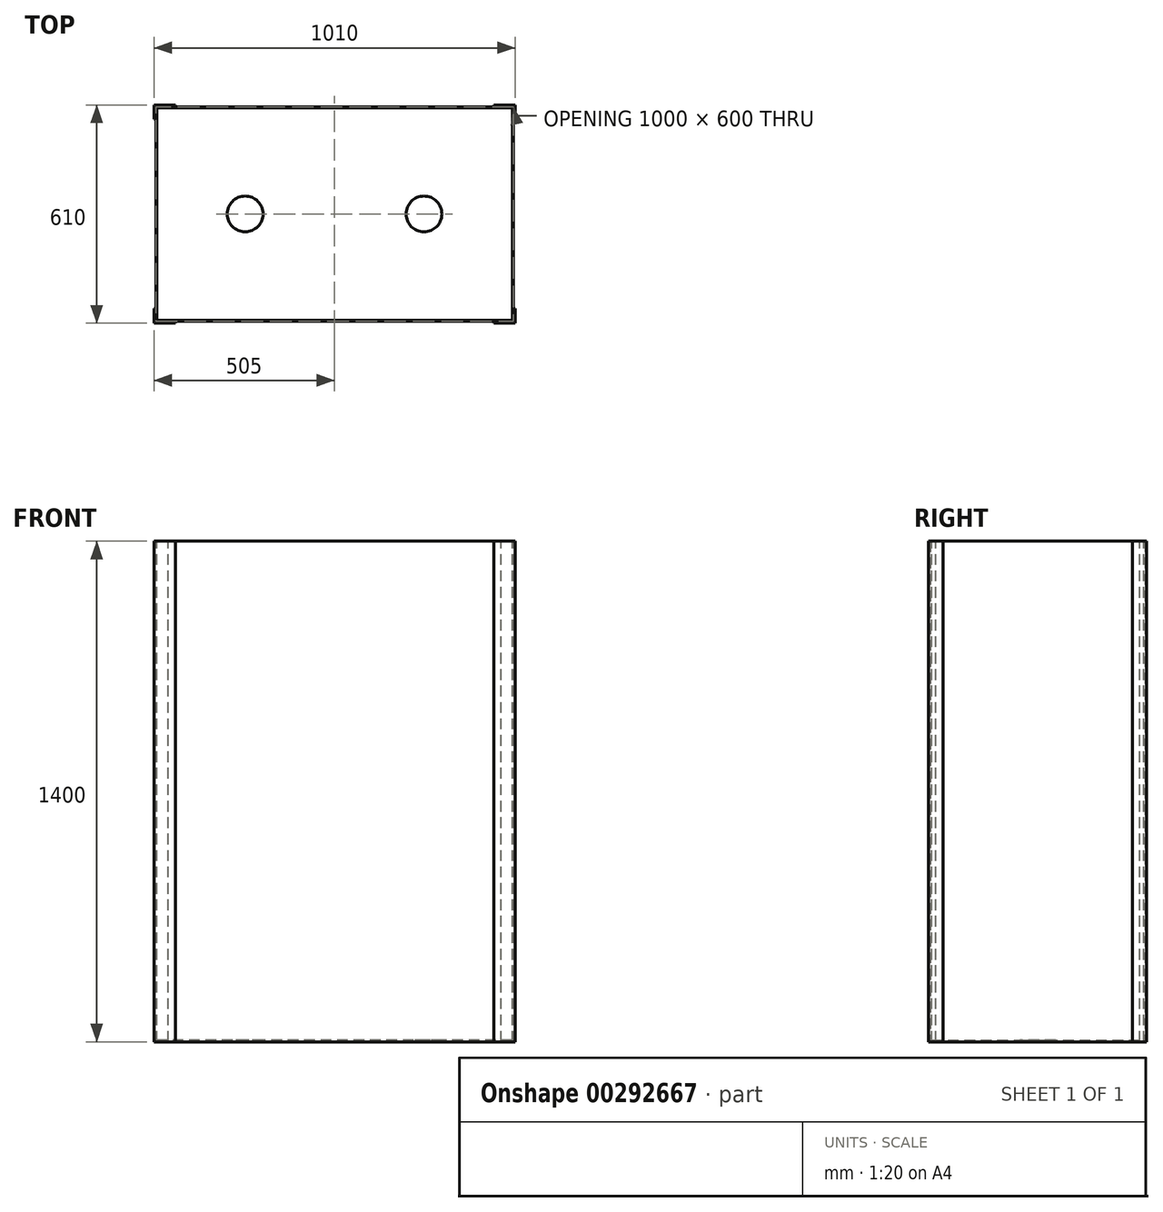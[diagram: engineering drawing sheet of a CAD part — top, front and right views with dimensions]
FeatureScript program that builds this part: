
annotation { "Feature Type Name" : "Feature", "Feature Type Description" : "" }
export const myFeature = defineFeature(function(context is Context, id is Id, definition is map)
    precondition{}
    {
        {
            var Q0;
            Q0=qCreatedBy(makeId("Top.planeOp"),FACE);
            cPlane(context, id + "F0", {"entities" : qUnion([Q0]), "cplaneType" : CPlaneType.OFFSET, "offset" : 1400 * mm, "width" : 150 * mm, "height" : 150 * mm});
        }
        {
            var Q0;
            Q0=qCreatedBy(makeId("Top.planeOp"),FACE);
            var sketch = newSketch(context, id + "F1", { "sketchPlane" : qUnion([Q0])});
            skLineSegment(sketch, "E0.bottom", {"start": v(500, 300) * mm, "end": v(-500, 300) * mm, "construction": true});
            skLineSegment(sketch, "E0.top", {"start": v(500, -300) * mm, "end": v(-500, -300) * mm, "construction": true});
            skLineSegment(sketch, "E0.left", {"start": v(500, 300) * mm, "end": v(500, -300) * mm, "construction": true});
            skLineSegment(sketch, "E0.right", {"start": v(-500, 300) * mm, "end": v(-500, -300) * mm, "construction": true});
            skPoint(sketch, "E0.middle", {"position": v(0, 0) * mm});
            skLineSegment(sketch, "E1", {"start": v(-505, 265) * mm, "end": v(-505, 305) * mm});
            skLineSegment(sketch, "E2", {"start": v(-505, 305) * mm, "end": v(-445, 305) * mm});
            skLineSegment(sketch, "E3.0", {"start": v(-500, 300) * mm, "end": v(-445, 300) * mm});
            skLineSegment(sketch, "E3.1", {"start": v(-500, 265) * mm, "end": v(-500, 300) * mm});
            skLineSegment(sketch, "E4", {"start": v(-445, 305) * mm, "end": v(-445, 300) * mm});
            skLineSegment(sketch, "E5", {"start": v(-505, 265) * mm, "end": v(-500, 265) * mm});
            skLineSegment(sketch, "E6", {"start": v(0, 0) * mm, "end": v(0, 347.4) * mm, "construction": true});
            skLineSegment(sketch, "E7", {"start": v(0, 0) * mm, "end": v(-536.75, 0) * mm, "construction": true});
            skPoint(sketch, "E7.endSnap0", {"position": v(-500, 0) * mm});
            skLineSegment(sketch, "E8.MirrorCS", {"start": v(445, 305) * mm, "end": v(445, 300) * mm});
            skLineSegment(sketch, "E9.MirrorCS", {"start": v(505, 265) * mm, "end": v(500, 265) * mm});
            skLineSegment(sketch, "E10.MirrorCS", {"start": v(500, 265) * mm, "end": v(500, 300) * mm});
            skLineSegment(sketch, "E11.MirrorCS", {"start": v(505, 265) * mm, "end": v(505, 305) * mm});
            skLineSegment(sketch, "E12.MirrorCS", {"start": v(505, 305) * mm, "end": v(445, 305) * mm});
            skLineSegment(sketch, "E13.MirrorCS", {"start": v(500, 300) * mm, "end": v(445, 300) * mm});
            skLineSegment(sketch, "E14.MirrorCS", {"start": v(445, -305) * mm, "end": v(445, -300) * mm});
            skLineSegment(sketch, "E15.MirrorCS", {"start": v(-505, -265) * mm, "end": v(-500, -265) * mm});
            skLineSegment(sketch, "E16.MirrorCS", {"start": v(-445, -305) * mm, "end": v(-445, -300) * mm});
            skLineSegment(sketch, "E17.MirrorCS", {"start": v(505, -265) * mm, "end": v(500, -265) * mm});
            skLineSegment(sketch, "E18.MirrorCS", {"start": v(-500, -300) * mm, "end": v(-445, -300) * mm});
            skLineSegment(sketch, "E19.MirrorCS", {"start": v(-505, -265) * mm, "end": v(-505, -305) * mm});
            skLineSegment(sketch, "E20.MirrorCS", {"start": v(500, -300) * mm, "end": v(445, -300) * mm});
            skLineSegment(sketch, "E21.MirrorCS", {"start": v(-505, -305) * mm, "end": v(-445, -305) * mm});
            skLineSegment(sketch, "E22.MirrorCS", {"start": v(505, -265) * mm, "end": v(505, -305) * mm});
            skLineSegment(sketch, "E23.MirrorCS", {"start": v(500, -265) * mm, "end": v(500, -300) * mm});
            skLineSegment(sketch, "E24.MirrorCS", {"start": v(505, -305) * mm, "end": v(445, -305) * mm});
            skLineSegment(sketch, "E25.MirrorCS", {"start": v(-500, -265) * mm, "end": v(-500, -300) * mm});
            skSolve(sketch);
        }
        {
            var Q0;
            Q0 = qSketchRegion(id + "F1", true);
            var Q1;
            Q1=qCreatedBy(id+"F0.planeOp",FACE);
            extrude(context, id + "F2", {"entities" : qUnion([Q0]), "endBound" : BoundingType.UP_TO_SURFACE, "endBoundEntityFace" : qUnion([Q1]), "depth" : 100 * mm});
        }
        {
            var Q0;
            Q0=qCreatedBy(id+"F0.planeOp",FACE);
            var sketch = newSketch(context, id + "F3", { "sketchPlane" : qUnion([Q0])});
            skLineSegment(sketch, "E26.bottom", {"start": v(-465, 300) * mm, "end": v(465, 300) * mm});
            skLineSegment(sketch, "E26.top", {"start": v(-465, 297) * mm, "end": v(465, 297) * mm});
            skLineSegment(sketch, "E26.left", {"start": v(-465, 300) * mm, "end": v(-465, 297) * mm});
            skLineSegment(sketch, "E26.right", {"start": v(465, 300) * mm, "end": v(465, 297) * mm});
            skLineSegment(sketch, "E27.bottom", {"start": v(500, 285) * mm, "end": v(497, 285) * mm});
            skLineSegment(sketch, "E27.top", {"start": v(500, -285) * mm, "end": v(497, -285) * mm});
            skLineSegment(sketch, "E27.left", {"start": v(500, 285) * mm, "end": v(500, -285) * mm});
            skLineSegment(sketch, "E27.right", {"start": v(497, 285) * mm, "end": v(497, -285) * mm});
            skLineSegment(sketch, "E28.bottom", {"start": v(465, -300) * mm, "end": v(-465, -300) * mm});
            skLineSegment(sketch, "E28.top", {"start": v(465, -297) * mm, "end": v(-465, -297) * mm});
            skLineSegment(sketch, "E28.left", {"start": v(465, -300) * mm, "end": v(465, -297) * mm});
            skLineSegment(sketch, "E28.right", {"start": v(-465, -300) * mm, "end": v(-465, -297) * mm});
            skLineSegment(sketch, "E29.bottom", {"start": v(-500, -285) * mm, "end": v(-497, -285) * mm});
            skLineSegment(sketch, "E29.top", {"start": v(-500, 285) * mm, "end": v(-497, 285) * mm});
            skLineSegment(sketch, "E29.left", {"start": v(-500, -285) * mm, "end": v(-500, 285) * mm});
            skLineSegment(sketch, "E29.right", {"start": v(-497, -285) * mm, "end": v(-497, 285) * mm});
            skSolve(sketch);
        }
        {
            var Q0;
            Q0 = qSketchRegion(id + "F3", true);
            var Q1;
            Q1=qCreatedBy(makeId("Top.planeOp"),FACE);
            extrude(context, id + "F4", {"entities" : qUnion([Q0]), "operationType" : NewBodyOperationType.ADD, "endBound" : BoundingType.UP_TO_SURFACE, "oppositeDirection" : true, "endBoundEntityFace" : qUnion([Q1]), "depth" : 25 * mm});
        }
        {
            var Q0;
            Q0=qCreatedBy(makeId("Top.planeOp"),FACE);
            var sketch = newSketch(context, id + "F5", { "sketchPlane" : qUnion([Q0])});
            skLineSegment(sketch, "E30.bottom", {"start": v(497, -297) * mm, "end": v(-497, -297) * mm});
            skLineSegment(sketch, "E30.top", {"start": v(497, 297) * mm, "end": v(-497, 297) * mm});
            skLineSegment(sketch, "E30.left", {"start": v(497, -297) * mm, "end": v(497, 297) * mm});
            skLineSegment(sketch, "E30.right", {"start": v(-497, -297) * mm, "end": v(-497, 297) * mm});
            skCircle(sketch, "E31", {"center": v(250, 0) * mm, "radius": 50 * mm});
            skCircle(sketch, "E32", {"center": v(-250, 0) * mm, "radius": 50 * mm});
            skSolve(sketch);
        }
        {
            var Q0;
            Q0=makeQuery(id+"F5.imprint","IMPRINT",FACE,{"disambiguationData":[TD([[makeQuery(id+"F5.imprint","IMPRINT",EDGE,{"derivedFrom":sQuery(id+"F5.wireOp",EDGE,"E30.bottom")}),-1.0]])]});
            extrude(context, id + "F6", {"entities" : qUnion([Q0]), "depth" : 5 * mm});
        }
    });
